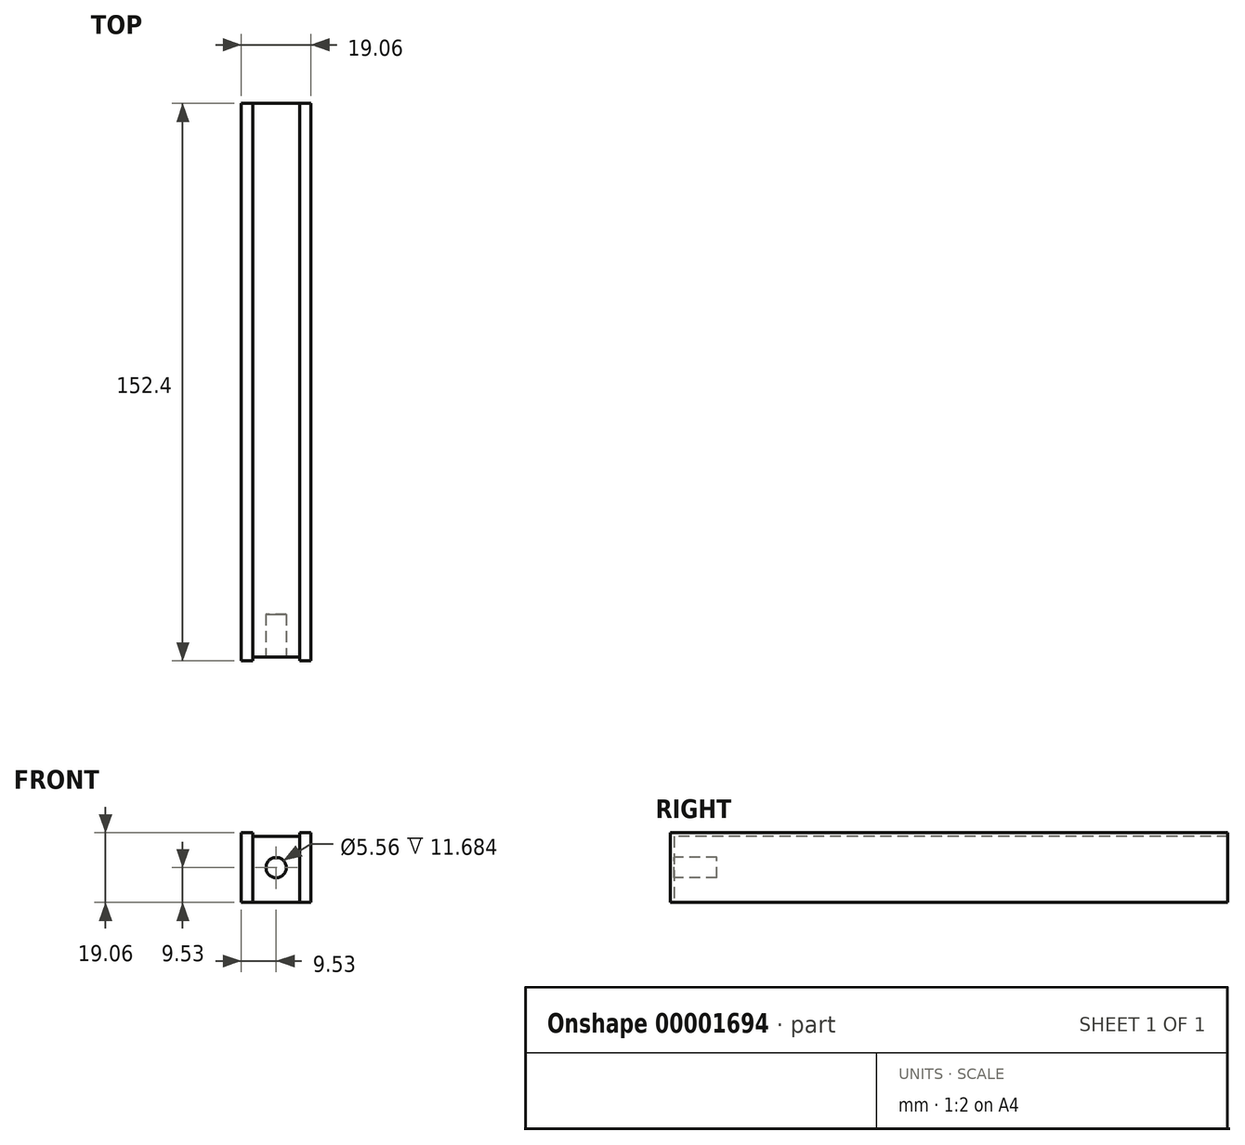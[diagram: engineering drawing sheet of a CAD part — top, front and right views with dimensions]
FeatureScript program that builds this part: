
annotation { "Feature Type Name" : "Feature", "Feature Type Description" : "" }
export const myFeature = defineFeature(function(context is Context, id is Id, definition is map)
    precondition{}
    {
        {
            var Q0;
            Q0=qCreatedBy(makeId("Front.planeOp"),FACE);
            var sketch = newSketch(context, id + "F0", { "sketchPlane" : qUnion([Q0])});
            skLineSegment(sketch, "E0.bottom", {"start": v(-9.53, 9.52) * mm, "end": v(9.52, 9.53) * mm});
            skLineSegment(sketch, "E0.top", {"start": v(-9.52, -9.53) * mm, "end": v(9.53, -9.52) * mm});
            skLineSegment(sketch, "E0.left", {"start": v(-9.53, 9.52) * mm, "end": v(-9.52, -9.53) * mm});
            skLineSegment(sketch, "E0.right", {"start": v(9.52, 9.53) * mm, "end": v(9.53, -9.52) * mm});
            skLineSegment(sketch, "E1", {"start": v(9.52, 9.53) * mm, "end": v(-9.52, -9.53) * mm, "construction": true});
            skSolve(sketch);
        }
        {
            var Q0;
            Q0=makeQuery(id+"F0.imprint","IMPRINT",FACE,{"disambiguationData":[TD([[makeQuery(id+"F0.imprint","IMPRINT",EDGE,{"derivedFrom":sQuery(id+"F0.wireOp",EDGE,"E0.bottom")}),-1.0]])]});
            extrude(context, id + "F1", {"entities" : qUnion([Q0]), "endBound" : BoundingType.SYMMETRIC, "depth" : 152.4 * mm});
        }
        {
            var Q0;
            Q0=makeQuery(id+"F1.opExtrude","SWEPT_FACE",FACE,{"disambiguationData":[OSD([sQuery(id+"F0.wireOp",EDGE,"E0.bottom")])]});
            var sketch = newSketch(context, id + "F2", { "sketchPlane" : qUnion([Q0])});
            skLineSegment(sketch, "E2.bottom", {"start": v(-6.4, 76.2) * mm, "end": v(6.4, 76.2) * mm});
            skLineSegment(sketch, "E2.top", {"start": v(-6.4, -76.2) * mm, "end": v(6.4, -76.2) * mm});
            skLineSegment(sketch, "E2.left", {"start": v(-6.4, 76.2) * mm, "end": v(-6.4, -76.2) * mm});
            skLineSegment(sketch, "E2.right", {"start": v(6.4, 76.2) * mm, "end": v(6.4, -76.2) * mm});
            skLineSegment(sketch, "E3", {"start": v(0, 76.2) * mm, "end": v(0, -76.2) * mm, "construction": true});
            skSolve(sketch);
        }
        {
            var Q0;
            Q0 = qSketchRegion(id + "F2", true);
            extrude(context, id + "F3", {"entities" : qUnion([Q0]), "operationType" : NewBodyOperationType.REMOVE, "oppositeDirection" : true, "depth" : 1.02 * mm});
        }
        {
            var Q0;
            Q0=makeQuery(id+"F1.opExtrude","CAP_FACE",FACE,{"disambiguationData":[OSD([sQuery(id+"F0.wireOp",EDGE,"E0.bottom"),sQuery(id+"F0.wireOp",EDGE,"E0.top"),sQuery(id+"F0.wireOp",EDGE,"E0.left"),sQuery(id+"F0.wireOp",EDGE,"E0.right")])],"isStart":false});
            var sketch = newSketch(context, id + "F4", { "sketchPlane" : qUnion([Q0])});
            skCircle(sketch, "E4", {"center": v(0, 0) * mm, "radius": 2.78 * mm});
            skSolve(sketch);
        }
        {
            var Q0;
            Q0 = qSketchRegion(id + "F4", true);
            extrude(context, id + "F5", {"entities" : qUnion([Q0]), "operationType" : NewBodyOperationType.REMOVE, "oppositeDirection" : true, "depth" : 12.7 * mm});
        }
        {
            var Q0;
            Q0=makeQuery(id+"F1.opExtrude","CAP_FACE",FACE,{"disambiguationData":[OSD([sQuery(id+"F0.wireOp",EDGE,"E0.bottom"),sQuery(id+"F0.wireOp",EDGE,"E0.top"),sQuery(id+"F0.wireOp",EDGE,"E0.left"),sQuery(id+"F0.wireOp",EDGE,"E0.right")])],"isStart":false});
            var sketch = newSketch(context, id + "F6", { "sketchPlane" : qUnion([Q0])});
            skLineSegment(sketch, "E5.bottom", {"start": v(-6.4, 8.5) * mm, "end": v(6.4, 8.5) * mm});
            skLineSegment(sketch, "E5.top", {"start": v(-6.4, -9.52) * mm, "end": v(6.4, -9.52) * mm});
            skLineSegment(sketch, "E5.left", {"start": v(-6.4, 8.5) * mm, "end": v(-6.4, -9.52) * mm});
            skLineSegment(sketch, "E5.right", {"start": v(6.4, 8.5) * mm, "end": v(6.4, -9.52) * mm});
            skSolve(sketch);
        }
        {
            var Q0;
            Q0 = qSketchRegion(id + "F6", true);
            extrude(context, id + "F7", {"entities" : qUnion([Q0]), "operationType" : NewBodyOperationType.REMOVE, "oppositeDirection" : true, "depth" : 1.02 * mm});
        }
    });
